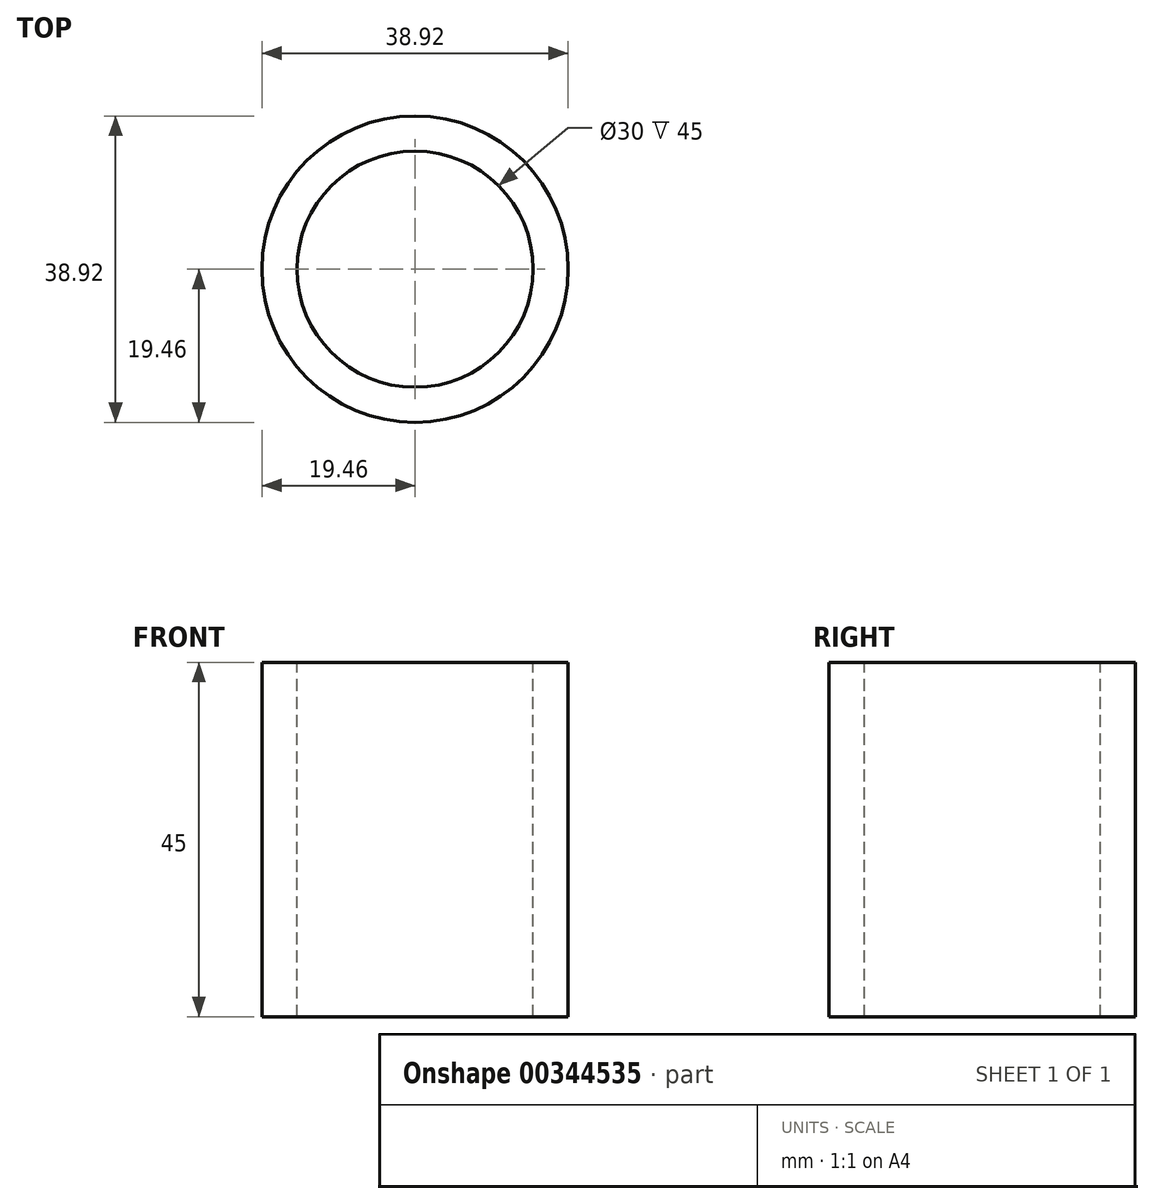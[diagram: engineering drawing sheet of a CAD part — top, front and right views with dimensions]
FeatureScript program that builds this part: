
annotation { "Feature Type Name" : "Feature", "Feature Type Description" : "" }
export const myFeature = defineFeature(function(context is Context, id is Id, definition is map)
    precondition{}
    {
        {
            var Q0;
            Q0=qCreatedBy(makeId("Top.planeOp"),FACE);
            var sketch = newSketch(context, id + "F0", { "sketchPlane" : qUnion([Q0])});
            skCircle(sketch, "E0", {"center": v(0, 0) * mm, "radius": 15 * mm});
            skCircle(sketch, "E1", {"center": v(0, 0) * mm, "radius": 19.46 * mm});
            skSolve(sketch);
        }
        {
            var Q0;
            Q0=makeQuery(id+"F0.imprint","IMPRINT",FACE,{"disambiguationData":[TD([[makeQuery(id+"F0.imprint","IMPRINT",EDGE,{"derivedFrom":sQuery(id+"F0.wireOp",EDGE,"E0")}),-1.0]])]});
            extrude(context, id + "F1", {"entities" : qUnion([Q0]), "oppositeDirection" : true, "depth" : 45 * mm});
        }
    });
